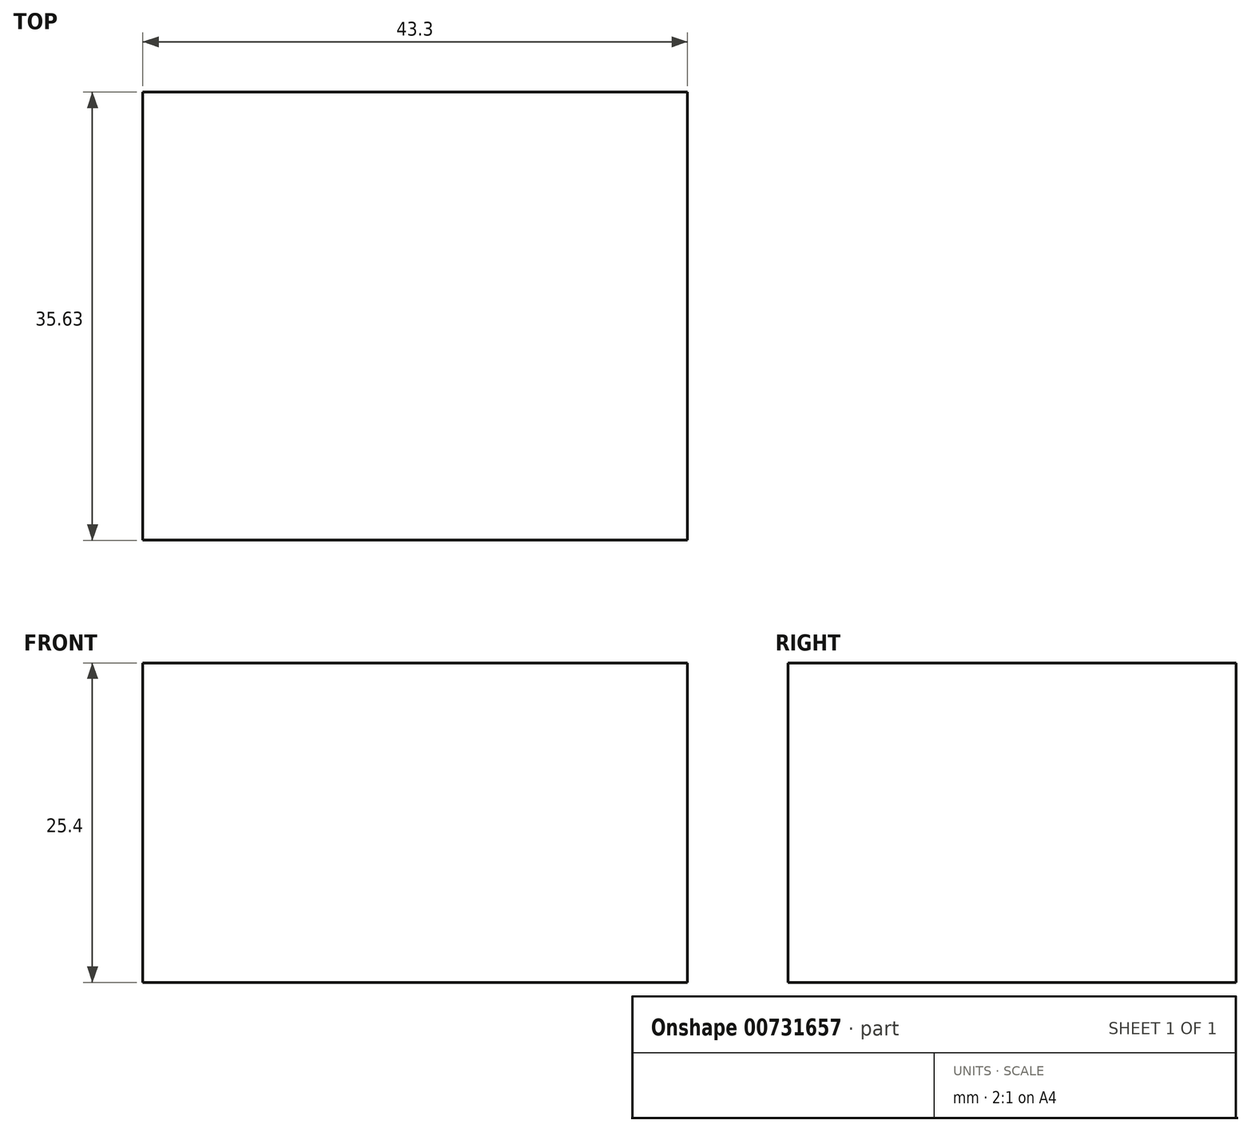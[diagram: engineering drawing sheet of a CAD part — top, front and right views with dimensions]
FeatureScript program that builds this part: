
annotation { "Feature Type Name" : "Feature", "Feature Type Description" : "" }
export const myFeature = defineFeature(function(context is Context, id is Id, definition is map)
    precondition{}
    {
        {
            var Q0;
            Q0=qCreatedBy(makeId("Top.planeOp"),FACE);
            var sketch = newSketch(context, id + "F0", { "sketchPlane" : qUnion([Q0])});
            skLineSegment(sketch, "E0.bottom", {"start": v(0, 0) * mm, "end": v(41.73, 0) * mm});
            skLineSegment(sketch, "E0.top", {"start": v(0, 0) * mm, "end": v(41.73, 0) * mm});
            skLineSegment(sketch, "E0.left", {"start": v(0, 0) * mm, "end": v(0, 0) * mm});
            skLineSegment(sketch, "E0.right", {"start": v(41.73, 0) * mm, "end": v(41.73, 0) * mm});
            skLineSegment(sketch, "E1.bottom", {"start": v(-30.9, 70.88) * mm, "end": v(12.41, 70.88) * mm});
            skLineSegment(sketch, "E1.top", {"start": v(-30.9, 35.25) * mm, "end": v(12.41, 35.25) * mm});
            skLineSegment(sketch, "E1.left", {"start": v(-30.9, 70.88) * mm, "end": v(-30.9, 35.25) * mm});
            skLineSegment(sketch, "E1.right", {"start": v(12.41, 70.88) * mm, "end": v(12.41, 35.25) * mm});
            skSolve(sketch);
        }
        {
            var Q0;
            Q0 = qSketchRegion(id + "F0", true);
            extrude(context, id + "F1", {"entities" : qUnion([Q0]), "depth" : 25.4 * mm, "offsetDistance" : 25.4 * mm});
        }
    });
